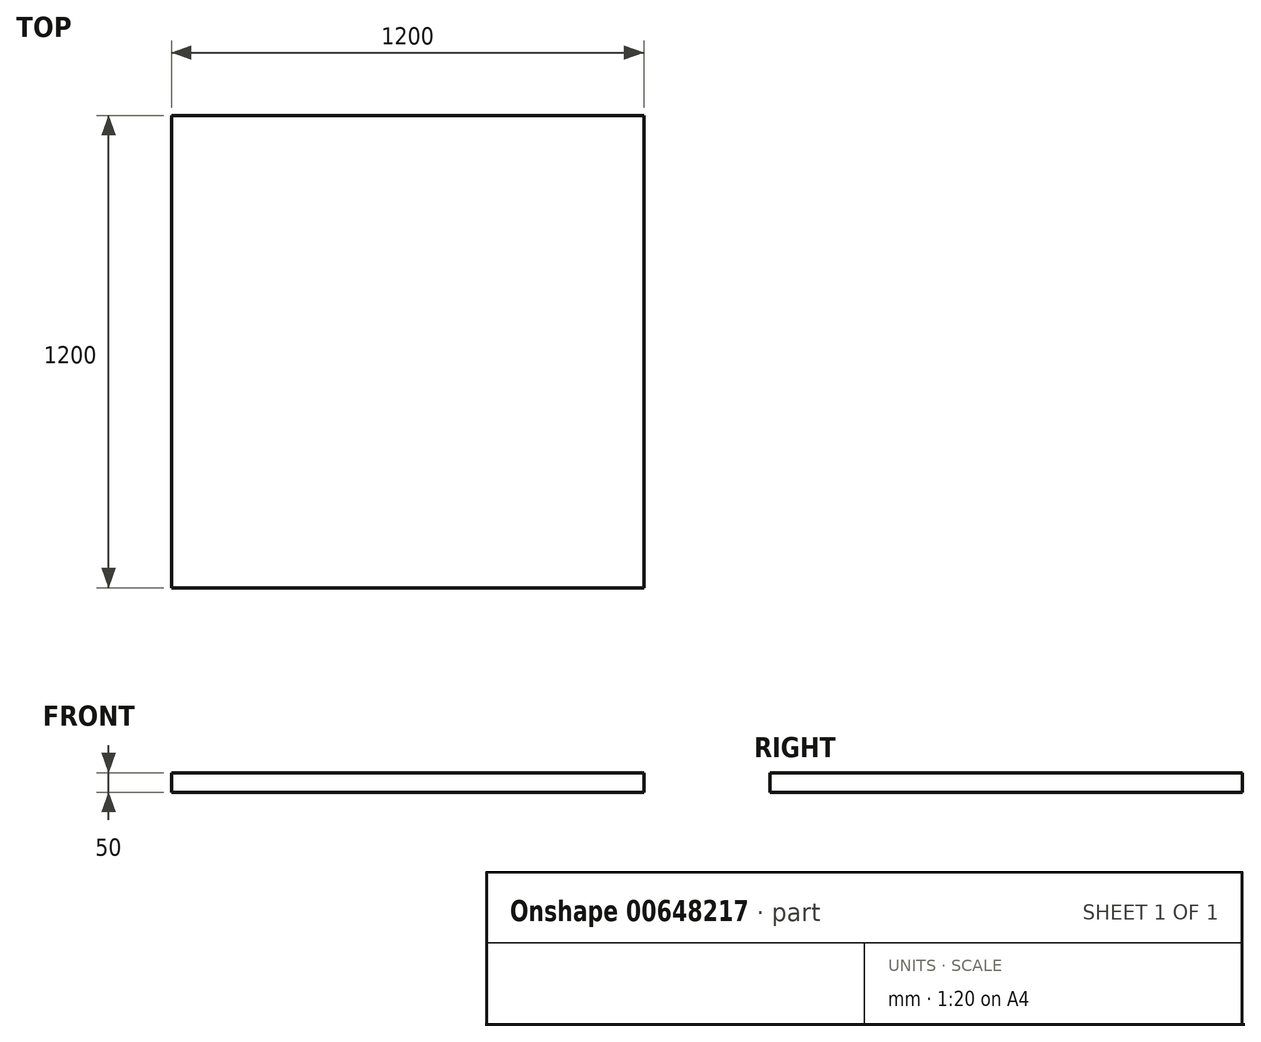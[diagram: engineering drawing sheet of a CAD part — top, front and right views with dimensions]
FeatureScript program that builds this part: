
annotation { "Feature Type Name" : "Feature", "Feature Type Description" : "" }
export const myFeature = defineFeature(function(context is Context, id is Id, definition is map)
    precondition{}
    {
        {
            var Q0;
            Q0=qCreatedBy(makeId("Top.planeOp"),FACE);
            var sketch = newSketch(context, id + "F0", { "sketchPlane" : qUnion([Q0])});
            skLineSegment(sketch, "E0.bottom", {"start": v(600, 599.4) * mm, "end": v(-600, 599.4) * mm});
            skLineSegment(sketch, "E0.top", {"start": v(600, -600.6) * mm, "end": v(-600, -600.6) * mm});
            skLineSegment(sketch, "E0.left", {"start": v(600, 599.4) * mm, "end": v(600, -600.6) * mm});
            skLineSegment(sketch, "E0.right", {"start": v(-600, 599.4) * mm, "end": v(-600, -600.6) * mm});
            skPoint(sketch, "E0.middle", {"position": v(0, -0.6) * mm});
            skSolve(sketch);
        }
        {
            var Q0;
            Q0=qSketchRegion(id+"F0",true);
            extrude(context, id + "F1", {"entities" : qUnion([Q0]), "depth" : 50 * mm, "offsetDistance" : 25 * mm});
        }
    });
